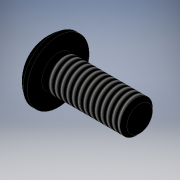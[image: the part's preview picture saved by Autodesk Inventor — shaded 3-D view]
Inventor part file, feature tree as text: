
AUTODESK INVENTOR PART (.ipt)
format: ipt  version: 2019 (Build 230136000, 136)  size: 157,696 bytes
history: native  units: mm
features: other x7, sketch x2, revolve x1, thread x1, extrude x1
ambient origin geometry x8: Origin, YZ Plane, XZ Plane, XY Plane, X Axis, Y Axis, Z Axis, Center Point
bodies: Solid1 (feature_tree)
feature tree (12):
  revolve  "Revolution1"  [1 undecoded]
  thread  "Thread1"  [1 undecoded]
  extrude  "Extrusion1"  [1 undecoded]
  other  "screw_XY"
  other  "screw_YZ"
  other  "screw_ZX"
  other  "screw_X"
  other  "screw_Y"
  other  "screw_Z"
  other  "screw_Center"
  sketch  "Sketch_1"  dims[d0=360.0deg d1=8.82658mm d2=0.0mm d3=1.87mm d4=0.0mm]
  sketch  "Sketch_2"  dims[d5=0.0mm]
note: 3 required parameter values undecoded (feature->parameter linkage not recoverable at this tier; creation-order binding heuristic only, values carry confidence <= 0.55)